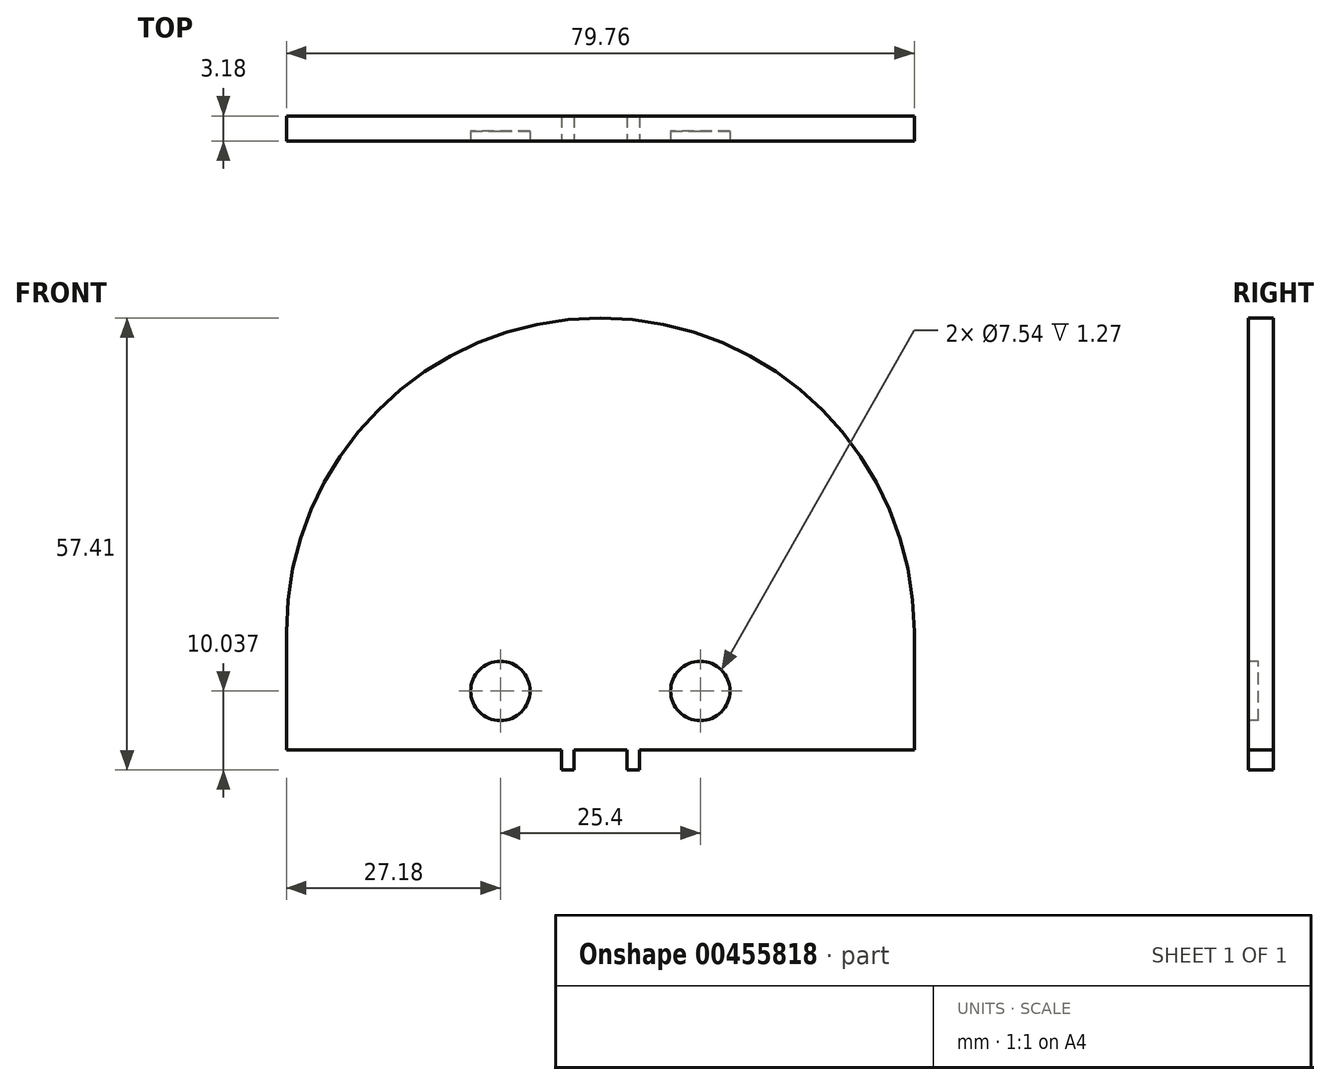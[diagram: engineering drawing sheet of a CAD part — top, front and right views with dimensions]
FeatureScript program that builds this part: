
annotation { "Feature Type Name" : "Feature", "Feature Type Description" : "" }
export const myFeature = defineFeature(function(context is Context, id is Id, definition is map)
    precondition{}
    {
        {
            var Q0;
            Q0=qCreatedBy(makeId("Front.planeOp"),FACE);
            var sketch = newSketch(context, id + "F0", { "sketchPlane" : qUnion([Q0])});
            skArc(sketch, "E0", {"start": v(-39.88, 0) * mm, "mid": v(0, 39.88) * mm, "end": v(39.88, 0) * mm});
            skLineSegment(sketch, "E1.top", {"start": v(-39.88, -14.99) * mm, "end": v(39.88, -14.99) * mm});
            skLineSegment(sketch, "E1.left", {"start": v(-39.88, 0) * mm, "end": v(-39.88, -14.99) * mm});
            skLineSegment(sketch, "E1.right", {"start": v(39.88, 0) * mm, "end": v(39.88, -14.99) * mm});
            skSolve(sketch);
        }
        {
            var Q0;
            Q0 = qSketchRegion(id + "F0", true);
            extrude(context, id + "F1", {"entities" : qUnion([Q0]), "depth" : 3.17 * mm, "offsetDistance" : 25.4 * mm});
        }
        {
            var Q0;
            Q0=makeQuery(id+"F1.opExtrude","CAP_FACE",FACE,{"disambiguationData":[OSD([sQuery(id+"F0.wireOp",EDGE,"E0"),sQuery(id+"F0.wireOp",EDGE,"E1.top"),sQuery(id+"F0.wireOp",EDGE,"E1.left"),sQuery(id+"F0.wireOp",EDGE,"E1.right")])],"isStart":false});
            var sketch = newSketch(context, id + "F2", { "sketchPlane" : qUnion([Q0])});
            skCircle(sketch, "E2", {"center": v(-12.7, -7.5) * mm, "radius": 3.77 * mm});
            skCircle(sketch, "E3", {"center": v(12.7, -7.5) * mm, "radius": 3.77 * mm});
            skSolve(sketch);
        }
        {
            var Q0;
            Q0 = qSketchRegion(id + "F2", true);
            extrude(context, id + "F3", {"entities" : qUnion([Q0]), "operationType" : NewBodyOperationType.REMOVE, "oppositeDirection" : true, "depth" : 1.27 * mm, "offsetDistance" : 25.4 * mm});
        }
        {
            var Q0;
            Q0=makeQuery(id+"F1.opExtrude","CAP_FACE",FACE,{"disambiguationData":[OSD([sQuery(id+"F0.wireOp",EDGE,"E0"),sQuery(id+"F0.wireOp",EDGE,"E1.top"),sQuery(id+"F0.wireOp",EDGE,"E1.left"),sQuery(id+"F0.wireOp",EDGE,"E1.right")])],"isStart":false});
            var sketch = newSketch(context, id + "F4", { "sketchPlane" : qUnion([Q0])});
            skLineSegment(sketch, "E4.bottom", {"start": v(-4.95, -14.99) * mm, "end": v(-3.37, -14.99) * mm});
            skLineSegment(sketch, "E4.top", {"start": v(-4.95, -17.53) * mm, "end": v(-3.37, -17.53) * mm});
            skLineSegment(sketch, "E4.left", {"start": v(-4.95, -14.99) * mm, "end": v(-4.95, -17.53) * mm});
            skLineSegment(sketch, "E4.right", {"start": v(-3.37, -14.99) * mm, "end": v(-3.37, -17.53) * mm});
            skLineSegment(sketch, "E5", {"start": v(0, 0) * mm, "end": v(0, -44.11) * mm, "construction": true});
            skLineSegment(sketch, "E6.MirrorCS", {"start": v(4.95, -14.99) * mm, "end": v(4.95, -17.53) * mm});
            skLineSegment(sketch, "E7.MirrorCS", {"start": v(4.95, -14.99) * mm, "end": v(3.37, -14.99) * mm});
            skLineSegment(sketch, "E8.MirrorCS", {"start": v(3.37, -14.99) * mm, "end": v(3.37, -17.53) * mm});
            skLineSegment(sketch, "E9.MirrorCS", {"start": v(4.95, -17.53) * mm, "end": v(3.37, -17.53) * mm});
            skSolve(sketch);
        }
        {
            var Q0;
            Q0 = qSketchRegion(id + "F4", true);
            extrude(context, id + "F5", {"entities" : qUnion([Q0]), "operationType" : NewBodyOperationType.ADD, "oppositeDirection" : true, "depth" : 3.17 * mm, "offsetDistance" : 25.4 * mm});
        }
    });
